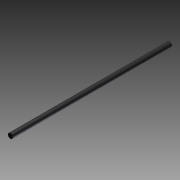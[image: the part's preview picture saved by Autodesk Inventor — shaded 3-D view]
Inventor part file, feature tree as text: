
AUTODESK INVENTOR PART (.ipt)
format: ipt  version: 2011 (Build 150239000, 239)  size: 73,216 bytes
history: native  units: mm (DEFAULTED — no unit token found)
features: extrude x1, thread x1, sketch x1
ambient origin geometry x8: Origin, YZ Plane, XZ Plane, XY Plane, X Axis, Y Axis, Z Axis, Center Point
bodies: Solid1 (feature_tree)
feature tree (3):
  extrude  "Extrusion1"  Depth=310.0mm TaperAngle=0.0deg
  thread  "Thread1"  [1 undecoded]
  sketch  "Sketch1"  dims[d0=9.525mm d1=310.0mm d2=0.0mm d3=10.0mm d4=0.0mm]
note: 1 required parameter value undecoded (feature->parameter linkage not recoverable at this tier; creation-order binding heuristic only, values carry confidence <= 0.55)
